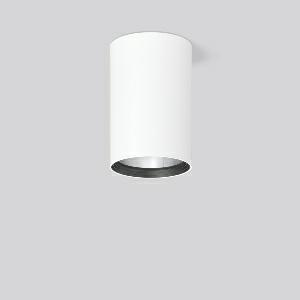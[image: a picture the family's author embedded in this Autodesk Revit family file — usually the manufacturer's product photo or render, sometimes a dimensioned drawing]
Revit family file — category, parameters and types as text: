
# Revit family: heledon_maxi_a_931219_002_c973
name_source: partatom
category: Lighting Fixtures
units: mm (PartAtom-declared; Revit-internal decimal feet)

## family parameters
Cut with Voids When Loaded = No
Host = Face
Light Source = No
Part Type = Normal
Room Calculation Point = No
Round Connector Dimension = Use Diameter
Shared = No

## types (1)
- HELEDON maxi A (1 x LED Modul 930, 3250 lm, 3000)
    Apparent Load = 25 VA
    Approval mark = CE
    CIE Flux Codes = 97 100 100 100 100
    Color Rendering = 90
    Color Temperature = 3000
    Default Elevation = 1800 mm
    Description = Series: HELEDON maxi
Cylindrical surface-mounted downlight. Housing: die-cast aluminium, powder-coated. Internal ceiling frame polycarbonate with bayonet mounting. Black plastic ring and recessed LED to prevent glare from the side. Optical assembly with reflector made of MIRO-Silver with 98% total light reflection for outstanding efficiency - can be changed without tools. Best colour rendering index Ra>90. Suitable for Ceiling mounting. Easy installation with a separate ceiling frame with bayonet mounting and plug connection. Driver integrated. Connected via plug-in connector. High quality converter without flickering and stroboscopic effect. The following accessories can be mounted without use of tools: interchangeable lenses, decorative glasses, honeycomb louvre, clear and frosted diffusers, white interchangeable plastic ring. 
Colour: traffic white, matt (RAL 9016)
Diameter: 123 mm
Height: 183 mm
Lamp: LED
Socket: without socket
Colour temperature: 3000K
Colour rendering index (CRI): 92
System power: 25 W
Rated luminous flux: 3250 lm
Luminous efficiency: 130 lm/W
Control gear: Regulated power supply
Protection class: I
Type of protection: IP 20
    Height = 183 mm
    Lamp = 1 x LED Modul 930
    Lamp Light Flux = 3250 lm
    Lamp count = 1
    Length = 123 mm
    Lifetime = 50000 h
    Luminous efficacy = 130 lm/W
    Manufacturer = RZB
    ModVariant = No
    Model = 931219.002
    Mounting Place = Ceiling
    Mounting Type = Surface mounted
    Number of Poles = 1
    OnlyDefault = Yes
    Power Factor = 1
    Product Name = HELEDON maxi A
    Product group = Surface mounted downlights
    ProductGroupID = 302
    Protection Class = Protection class I
    Protection Degree = IP 20
    RLX_Detail_Level = 1
    RLX_Emergency_Light_Flux = 0 lm
    RLX_Emergency_Type = 0
    RLX_Emergency_Type_DB = No
    RlxData = <blob elided: 96909 chars, md5=15061ef8>
    Socket = socket
    Standby Power = 0 W
    System Light Flux = 3250 lm
    System Power = 25 W
    Type Comments = Product without accessories
    Type Image = 931192.002.jpg
    URL = http://relux.com
    VarID = ---
    Voltage = 230 V
    Voltage Range = 220-240 V
    Weight = 0.00 kg
    Width = 0 mm  [stored 0 ft]

note: [stored X ft] marks values corroborated as IEEE doubles in the binary element streams (Revit-internal decimal feet)

## geometry (parser evidence)
native form markers: Blend x4, Sweep x11
no freeform markers — native parametric forms only
